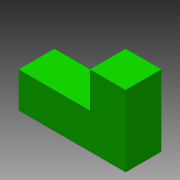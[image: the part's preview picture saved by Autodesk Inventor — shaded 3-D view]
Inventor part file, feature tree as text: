
AUTODESK INVENTOR PART (.ipt)
format: ipt  version: 2013 (Build 170138000, 138)  size: 89,600 bytes
history: native  units: in
note: dims shown in document units (in); Inventor stores cm internally (conversion verified against a paired STEP export)
features: extrude x2, sketch x2
ambient origin geometry x8: Origin, YZ Plane, XZ Plane, XY Plane, X Axis, Y Axis, Z Axis, Center Point
bodies: Solid1 (feature_tree)
feature tree (4):
  extrude  "Extrusion1"  Depth=0.75in
  extrude  "Extrusion2"  Depth=0.75in
  sketch  "Sketch1"  dims[d0=2.25in d1=0.75in]
  sketch  "Sketch2"  dims[d2=0.75in d3=0.0in d4=0.75in d5=0.75in d6=0.75in d7=0.0in]
